# Revit family: NBS_WallgateLtd_PrxmtySnsrCtrlUnits_WDC200
name_source: partatom
category: Mechanical Equipment
revit_build: Autodesk Revit 2014 (Build: 20130709_2115(x64)
units: mm (PartAtom-declared; Revit-internal decimal feet)

## types (1)
- WDC200
    AccessoryOptions = CISTFV Electronic cisterns, FVA Non-Potable Direct Flush Valves, DFKIT Potable Direct Flush Valves, WVC Flush Valve Cables, PBA Piezo Touch Buttons, PBA-IR Infra-Red Activation Sensors, WVPB Basin Water Valve Pack, WVPS Shower Water Valve Pack, CLS Key Switches
    ApplicationOptions = Central or stand alone
    AssetType = Fixed
    BIMObjectName = NBS_WallgateLtd_ProximitySensorControlUnits_WDC200
    ControlType = Unset
    Cost = 0 $
    Description = Fully programmable eight channel electronic controller to manage all sanitary ware within two adjacent rooms, typically; 2 x Basins, 2 x WC's & 2 x Shower
    DurationUnit = year
    ElectricalDeviceNominalPower = 50
    Features = Highly energy and water efficient, easily programmable - locally or networked
    HasProtectiveEarth = Yes
    IP_Code = IP55
    IfcExportAs = IfcControllerType
    IfcExportType = NOTDEFINED
    InstallationDate = 1900-12-31T23:59:59
    ManufacturerName = Wallgate Ltd
    ManufacturerURL = www.wallgate.com
    ModelNumber = WDC200
    Mounting = Wall mounted
    NBSCertification = www.nationalbimlibrary.com/cert/qjg1jsvx
    NBSDescription = Proximity sensor control units
    NBSReference = 45-35-70/422
    Name = ProximitySensorControlUnits_WDC200_WallgateLtd
    NominalCurrent = 1
    NominalFrequencyRange = 50.0 , 60.0
    NominalHeight = 150 mm
    NominalLength = 200 mm
    NominalVoltage = 110.0 , 240.0
    NominalWidth = 90 mm
    NumberOfPoles = 0
    OutletNumber = 8
    PhaseAngle = 0.00°
    ProductInformation = www.wallgate.com/products/washroom-controls/wdc-electronic-controller-range
    SensorControlMaterial = NBS_Concept
    SignalFactor = 0
    SignalOffset = 0
    SignalTime = 0
    ThirdPartyCertification = CE marked, SAA Approved
    Uniclass2 = 45-51-53/465
    UsageCurrent = 1
    Version = 3
    WarrantyDurationParts = 1
    WarrantyDurationUnit = year
    WarrantyStartDate = 1900-12-31T23:59:59
    Weight = 1.7 kg

## geometry (parser evidence)
native form markers: Sweep x1
no freeform markers — native parametric forms only
